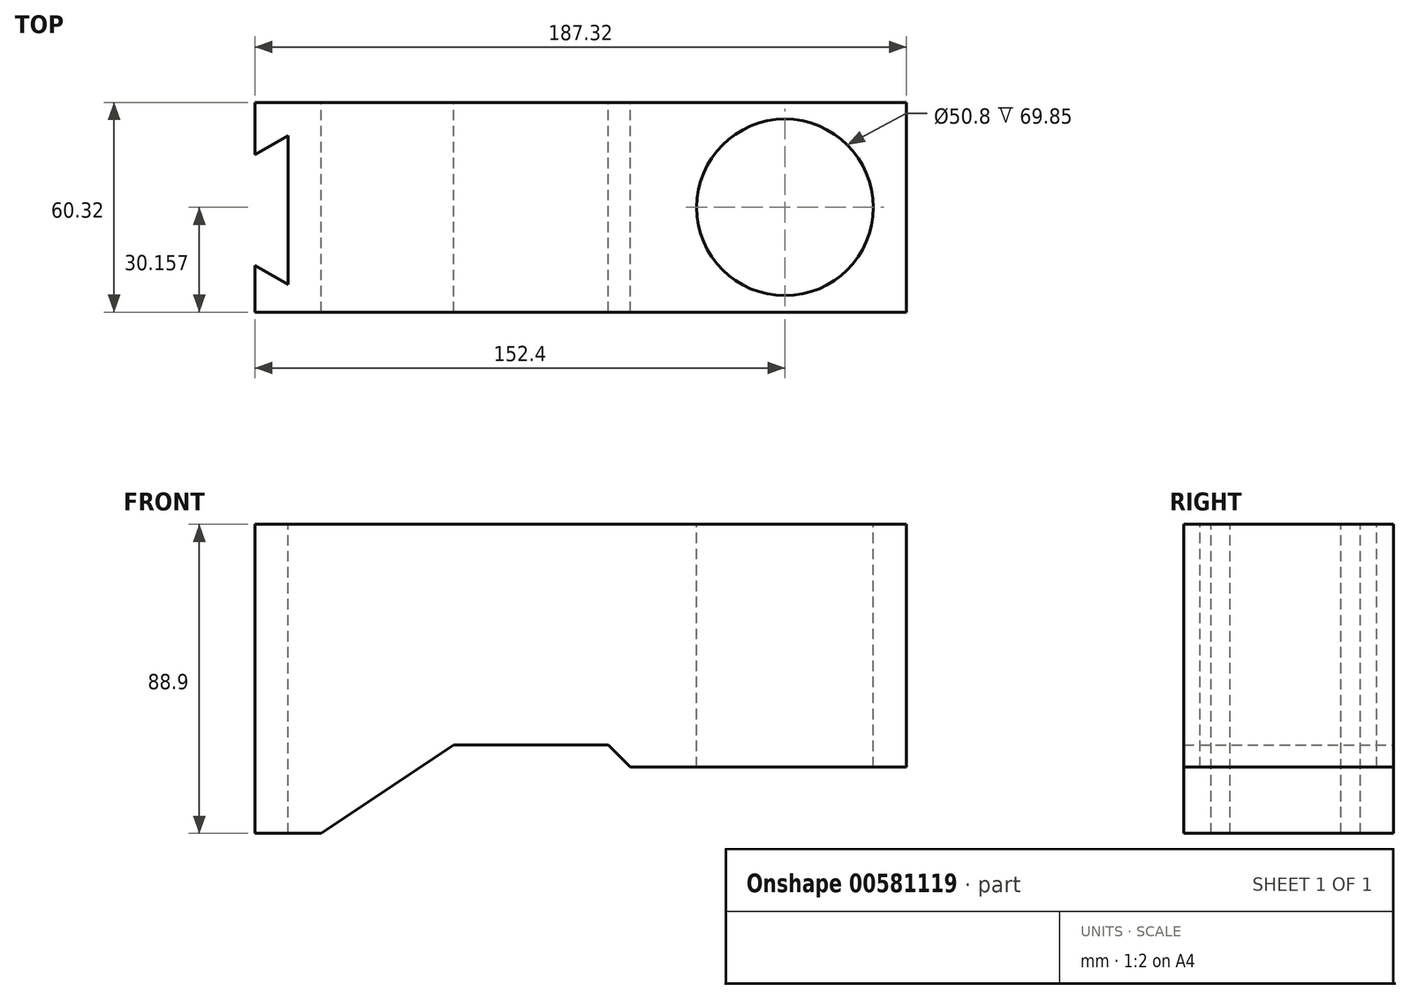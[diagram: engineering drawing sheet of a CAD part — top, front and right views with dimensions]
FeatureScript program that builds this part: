
annotation { "Feature Type Name" : "Feature", "Feature Type Description" : "" }
export const myFeature = defineFeature(function(context is Context, id is Id, definition is map)
    precondition{}
    {
        {
            var Q0;
            Q0=qCreatedBy(makeId("Front.planeOp"),FACE);
            var sketch = newSketch(context, id + "F0", { "sketchPlane" : qUnion([Q0])});
            skLineSegment(sketch, "E0", {"start": v(0, 0) * mm, "end": v(0, 88.9) * mm});
            skLineSegment(sketch, "E1", {"start": v(0, 88.9) * mm, "end": v(187.33, 88.9) * mm});
            skLineSegment(sketch, "E2", {"start": v(187.33, 88.9) * mm, "end": v(187.33, 19.05) * mm});
            skLineSegment(sketch, "E3", {"start": v(187.33, 19.05) * mm, "end": v(107.95, 19.05) * mm});
            skLineSegment(sketch, "E4", {"start": v(107.95, 19.05) * mm, "end": v(101.6, 25.4) * mm});
            skLineSegment(sketch, "E5", {"start": v(101.6, 25.4) * mm, "end": v(57.15, 25.4) * mm});
            skLineSegment(sketch, "E6", {"start": v(57.15, 25.4) * mm, "end": v(19.05, 0) * mm});
            skLineSegment(sketch, "E7", {"start": v(19.05, 0) * mm, "end": v(0, 0) * mm});
            skSolve(sketch);
        }
        {
            var Q0;
            Q0=makeQuery(id+"F0.imprint","IMPRINT",FACE,{"disambiguationData":[TD([[makeQuery(id+"F0.imprint","IMPRINT",EDGE,{"derivedFrom":sQuery(id+"F0.wireOp",EDGE,"E0")}),-1.0]])]});
            extrude(context, id + "F1", {"entities" : qUnion([Q0]), "depth" : 60.32 * mm, "offsetDistance" : 25.4 * mm});
        }
        {
            var Q0;
            Q0=makeQuery(id+"F1.opExtrude","SWEPT_FACE",FACE,{"disambiguationData":[OSD([sQuery(id+"F0.wireOp",EDGE,"E1")])]});
            var sketch = newSketch(context, id + "F2", { "sketchPlane" : qUnion([Q0])});
            skPoint(sketch, "E8", {"position": v(152.4, -30.16) * mm});
            skPoint(sketch, "E8.positionSnap0", {"position": v(187.33, -30.16) * mm});
            skSolve(sketch);
        }
        {
            var Q0;
            Q0=sQuery(id+"F2.wireOp",VERTEX,"E8");
            var Q1;
            Q1=makeQuery(id+"F1.opExtrude","SWEPT_BODY",BODY,{"disambiguationData":[OSD([sQuery(id+"F0.wireOp",EDGE,"E0"),sQuery(id+"F0.wireOp",EDGE,"E1"),sQuery(id+"F0.wireOp",EDGE,"E2"),sQuery(id+"F0.wireOp",EDGE,"E3"),sQuery(id+"F0.wireOp",EDGE,"E4"),sQuery(id+"F0.wireOp",EDGE,"E5"),sQuery(id+"F0.wireOp",EDGE,"E6"),sQuery(id+"F0.wireOp",EDGE,"E7")])]});
            hole(context, id + "F3", {"style" : HoleStyle.SIMPLE, "endStyle" : HoleEndStyle.THROUGH, "holeDiameter" : 50.8 * mm, "majorDiameter" : 6.35 * mm, "isTappedThrough" : true, "tappedDepth" : 12.7 * mm, "tapClearance" : 3, "locations" : qUnion([Q0]), "scope" : qUnion([Q1])});
        }
        {
            var Q0;
            Q0=makeQuery(id+"F1.opExtrude","SWEPT_FACE",FACE,{"disambiguationData":[OSD([sQuery(id+"F0.wireOp",EDGE,"E1")])]});
            var sketch = newSketch(context, id + "F4", { "sketchPlane" : qUnion([Q0])});
            skLineSegment(sketch, "E9", {"start": v(0, -15.02) * mm, "end": v(9.53, -9.52) * mm});
            skLineSegment(sketch, "E10", {"start": v(9.53, -9.52) * mm, "end": v(9.53, -52.39) * mm});
            skLineSegment(sketch, "E11", {"start": v(9.53, -52.39) * mm, "end": v(0, -46.89) * mm});
            skLineSegment(sketch, "E12", {"start": v(0, -46.89) * mm, "end": v(0, -15.02) * mm});
            skSolve(sketch);
        }
        {
            var Q0;
            Q0=makeQuery(id+"F4.imprint","IMPRINT",FACE,{"disambiguationData":[TD([[makeQuery(id+"F4.imprint","IMPRINT",EDGE,{"derivedFrom":sQuery(id+"F4.wireOp",EDGE,"E9")}),-1.0]])]});
            extrude(context, id + "F5", {"entities" : qUnion([Q0]), "operationType" : NewBodyOperationType.REMOVE, "endBound" : BoundingType.THROUGH_ALL, "oppositeDirection" : true, "depth" : 25.4 * mm, "offsetDistance" : 25.4 * mm});
        }
    });
